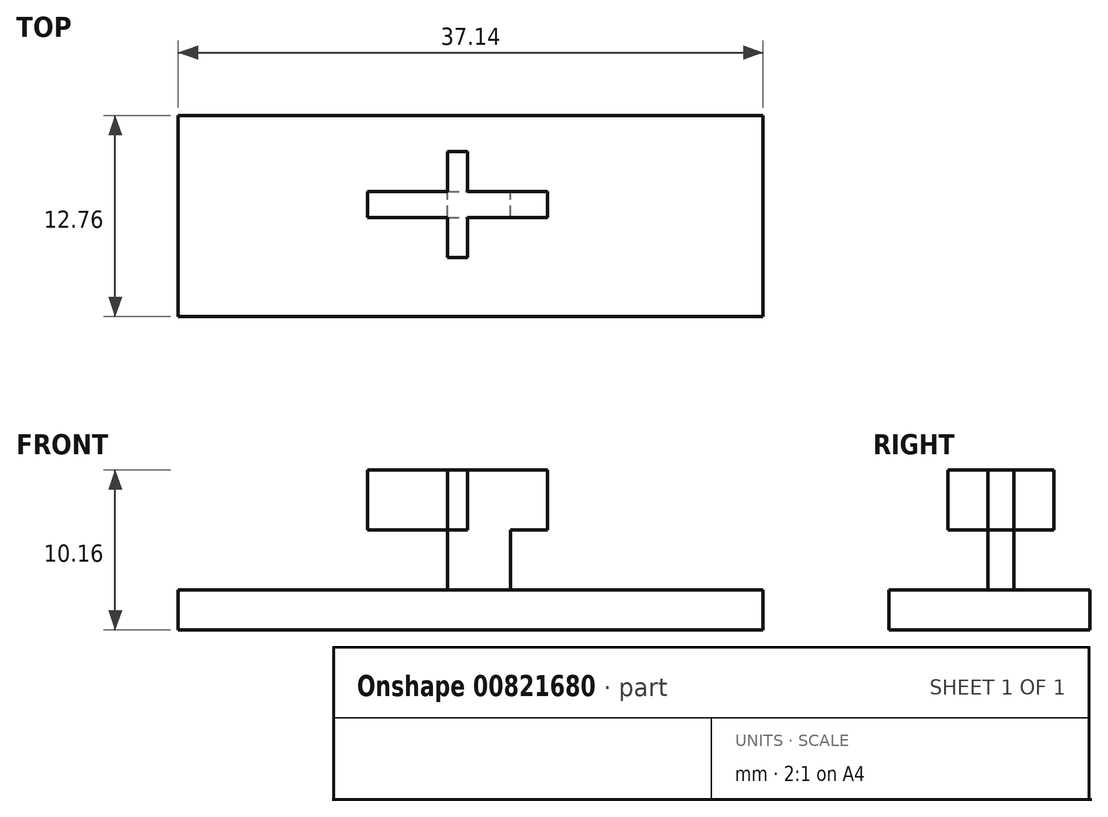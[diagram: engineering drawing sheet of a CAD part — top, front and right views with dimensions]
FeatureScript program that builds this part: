
annotation { "Feature Type Name" : "Feature", "Feature Type Description" : "" }
export const myFeature = defineFeature(function(context is Context, id is Id, definition is map)
    precondition{}
    {
        {
            var Q0;
            Q0=qCreatedBy(makeId("Top.planeOp"),FACE);
            var sketch = newSketch(context, id + "F0", { "sketchPlane" : qUnion([Q0])});
            skLineSegment(sketch, "E0.bottom", {"start": v(-19.4, -2.19) * mm, "end": v(17.74, -2.19) * mm});
            skLineSegment(sketch, "E0.top", {"start": v(-19.4, -14.95) * mm, "end": v(17.74, -14.95) * mm});
            skLineSegment(sketch, "E0.left", {"start": v(-19.4, -2.19) * mm, "end": v(-19.4, -14.95) * mm});
            skLineSegment(sketch, "E0.right", {"start": v(17.74, -2.19) * mm, "end": v(17.74, -14.95) * mm});
            skSolve(sketch);
        }
        {
            var Q0;
            Q0=makeQuery(id+"F0.imprint","IMPRINT",FACE,{"disambiguationData":[TD([[makeQuery(id+"F0.imprint","IMPRINT",EDGE,{"derivedFrom":sQuery(id+"F0.wireOp",EDGE,"E0.bottom")}),-1.0]])]});
            extrude(context, id + "F1", {"entities" : qUnion([Q0]), "depth" : 2.54 * mm, "offsetDistance" : 25.4 * mm});
        }
        {
            var Q0;
            Q0=makeQuery(id+"F1.opExtrude","CAP_FACE",FACE,{"disambiguationData":[OSD([sQuery(id+"F0.wireOp",EDGE,"E0.bottom"),sQuery(id+"F0.wireOp",EDGE,"E0.top"),sQuery(id+"F0.wireOp",EDGE,"E0.left"),sQuery(id+"F0.wireOp",EDGE,"E0.right")])],"isStart":false});
            var sketch = newSketch(context, id + "F2", { "sketchPlane" : qUnion([Q0])});
            skLineSegment(sketch, "E1.bottom", {"start": v(-2.3, -8.67) * mm, "end": v(1.7, -8.67) * mm});
            skLineSegment(sketch, "E1.top", {"start": v(-2.3, -7.02) * mm, "end": v(1.7, -7.02) * mm});
            skLineSegment(sketch, "E1.left", {"start": v(-2.3, -8.67) * mm, "end": v(-2.3, -7.02) * mm});
            skLineSegment(sketch, "E1.right", {"start": v(1.7, -8.67) * mm, "end": v(1.7, -7.02) * mm});
            skSolve(sketch);
        }
        {
            var Q0;
            Q0=makeQuery(id+"F2.imprint","IMPRINT",FACE,{"disambiguationData":[TD([[makeQuery(id+"F2.imprint","IMPRINT",EDGE,{"derivedFrom":sQuery(id+"F2.wireOp",EDGE,"E1.bottom")}),1.0]])]});
            extrude(context, id + "F3", {"entities" : qUnion([Q0]), "operationType" : NewBodyOperationType.ADD, "depth" : 3.8 * mm, "offsetDistance" : 25.4 * mm});
        }
        {
            var Q0;
            Q0=makeQuery(id+"F3.opExtrude","CAP_FACE",FACE,{"disambiguationData":[OSD([sQuery(id+"F2.wireOp",EDGE,"E1.bottom"),sQuery(id+"F2.wireOp",EDGE,"E1.top"),sQuery(id+"F2.wireOp",EDGE,"E1.left"),sQuery(id+"F2.wireOp",EDGE,"E1.right")])],"isStart":false});
            var sketch = newSketch(context, id + "F4", { "sketchPlane" : qUnion([Q0])});
            skLineSegment(sketch, "E2", {"start": v(-2.3, -7.02) * mm, "end": v(-2.3, -4.48) * mm});
            skLineSegment(sketch, "E3", {"start": v(-2.3, -8.67) * mm, "end": v(-2.3, -11.2) * mm});
            skLineSegment(sketch, "E4", {"start": v(-2.3, -7.02) * mm, "end": v(4.04, -7.02) * mm});
            skLineSegment(sketch, "E5", {"start": v(4.04, -7.02) * mm, "end": v(4.04, -8.67) * mm});
            skLineSegment(sketch, "E6", {"start": v(4.04, -8.67) * mm, "end": v(-2.3, -8.67) * mm});
            skLineSegment(sketch, "E7", {"start": v(-2.3, -7.02) * mm, "end": v(-7.39, -7.02) * mm});
            skLineSegment(sketch, "E8", {"start": v(-7.39, -7.02) * mm, "end": v(-7.39, -8.67) * mm});
            skLineSegment(sketch, "E9", {"start": v(-7.39, -8.67) * mm, "end": v(-2.3, -8.67) * mm});
            skLineSegment(sketch, "E10", {"start": v(-2.3, -4.48) * mm, "end": v(-1.04, -4.48) * mm});
            skLineSegment(sketch, "E11", {"start": v(-1.04, -4.48) * mm, "end": v(-1.04, -7.02) * mm});
            skLineSegment(sketch, "E12", {"start": v(-2.3, -11.2) * mm, "end": v(-1.04, -11.2) * mm});
            skLineSegment(sketch, "E13", {"start": v(-1.04, -11.2) * mm, "end": v(-1.04, -4.48) * mm});
            skSolve(sketch);
        }
        {
            var Q0;
            Q0=makeQuery(id+"F4.imprint","IMPRINT",FACE,{"disambiguationData":[TD([[makeQuery(id+"F4.imprint","IMPRINT",EDGE,{"derivedFrom":sQuery(id+"F4.wireOp",EDGE,"E7")}),1.0]])]});
            var Q1;
            {var subQ1=makeQuery(id+"F3.opExtrude","CAP_EDGE",EDGE,{"disambiguationData":[OSD([sQuery(id+"F2.wireOp",EDGE,"E1.left")])],"isStart":false});Q1=makeQuery(id+"F4.imprint","IMPRINT",FACE,{"disambiguationData":[TD([[makeQuery(id+"F4.imprint","IMPRINT",EDGE,{"derivedFrom":subQ1}),-1.0]])]});}
            var Q2;
            {var subQ1=makeQuery(id+"F3.opExtrude","CAP_EDGE",EDGE,{"disambiguationData":[OSD([sQuery(id+"F2.wireOp",EDGE,"E1.right")])],"isStart":false});Q2=makeQuery(id+"F4.imprint","IMPRINT",FACE,{"disambiguationData":[TD([[makeQuery(id+"F4.imprint","IMPRINT",EDGE,{"derivedFrom":subQ1}),1.0]])]});}
            var Q3;
            {var subQ2=sQuery(id+"F4.wireOp",EDGE,"E5");Q3=makeQuery(id+"F4.imprint","IMPRINT",FACE,{"disambiguationData":[TD([[makeQuery(id+"F4.imprint","IMPRINT",EDGE,{"derivedFrom":subQ2}),-1.0]])]});}
            var Q4;
            {var subQ0=sQuery(id+"F4.wireOp",EDGE,"E2");Q4=makeQuery(id+"F4.imprint","IMPRINT",FACE,{"disambiguationData":[TD([[makeQuery(id+"F4.imprint","IMPRINT",EDGE,{"derivedFrom":subQ0}),-1.0]])]});}
            var Q5;
            {var subQ0=sQuery(id+"F4.wireOp",EDGE,"E3");Q5=makeQuery(id+"F4.imprint","IMPRINT",FACE,{"disambiguationData":[TD([[makeQuery(id+"F4.imprint","IMPRINT",EDGE,{"derivedFrom":subQ0}),1.0]])]});}
            extrude(context, id + "F5", {"entities" : qUnion([Q0, Q1, Q2, Q3, Q4, Q5]), "operationType" : NewBodyOperationType.ADD, "depth" : 3.8 * mm, "offsetDistance" : 25.4 * mm});
        }
    });
